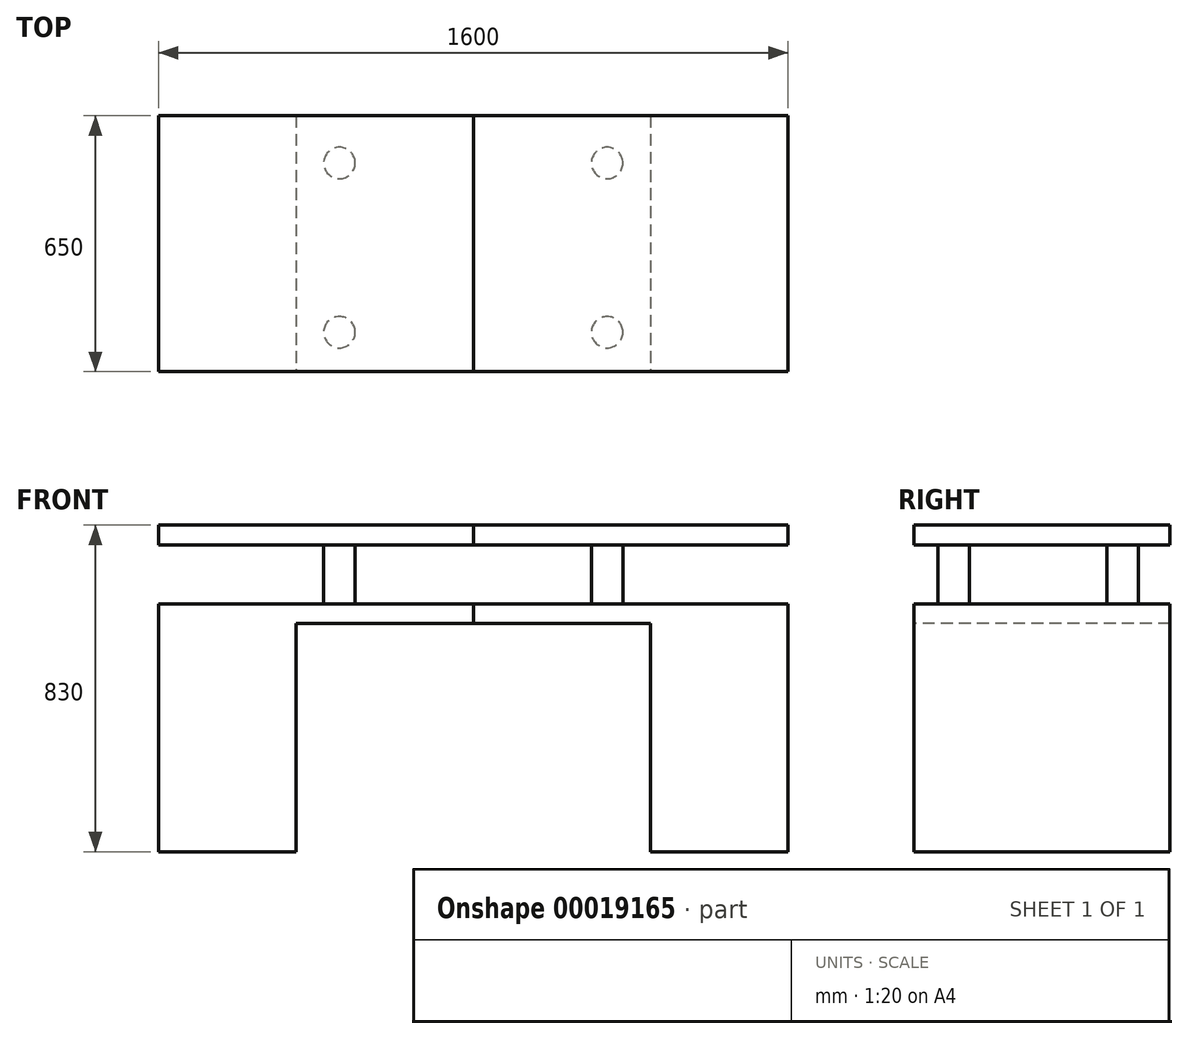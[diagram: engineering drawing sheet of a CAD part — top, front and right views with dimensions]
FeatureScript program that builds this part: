
annotation { "Feature Type Name" : "Feature", "Feature Type Description" : "" }
export const myFeature = defineFeature(function(context is Context, id is Id, definition is map)
    precondition{}
    {
        {
            var Q0;
            Q0=qCreatedBy(makeId("Top.planeOp"),FACE);
            var sketch = newSketch(context, id + "F0", { "sketchPlane" : qUnion([Q0])});
            skLineSegment(sketch, "E0.bottom", {"start": v(0, 0) * mm, "end": v(-800, 0) * mm});
            skLineSegment(sketch, "E0.top", {"start": v(0, -650) * mm, "end": v(-800, -650) * mm});
            skLineSegment(sketch, "E0.left", {"start": v(0, 0) * mm, "end": v(0, -650) * mm});
            skLineSegment(sketch, "E0.right", {"start": v(-800, 0) * mm, "end": v(-800, -650) * mm});
            skSolve(sketch);
        }
        {
            var Q0;
            Q0=qCreatedBy(makeId("Top.planeOp"),FACE);
            cPlane(context, id + "F1", {"entities" : qUnion([Q0]), "cplaneType" : CPlaneType.OFFSET, "offset" : 150 * mm, "width" : 150 * mm, "height" : 150 * mm});
        }
        {
            var Q0;
            Q0=qCreatedBy(id+"F1.planeOp",FACE);
            cPlane(context, id + "F2", {"entities" : qUnion([Q0]), "cplaneType" : CPlaneType.OFFSET, "offset" : 50 * mm, "width" : 150 * mm, "height" : 150 * mm});
        }
        {
            var Q0;
            Q0 = qSketchRegion(id + "F0", true);
            var Q1;
            Q1=qCreatedBy(id+"F2.planeOp",FACE);
            extrude(context, id + "F3", {"entities" : qUnion([Q0]), "oppositeDirection" : true, "depth" : 50 * mm, "hasSecondDirection" : true, "secondDirectionBound" : BoundingType.UP_TO_SURFACE, "secondDirectionOppositeDirection" : false, "secondDirectionBoundEntityFace" : qUnion([Q1]), "secondDirectionDepth" : 300 * mm});
        }
        {
            var Q0;
            Q0 = qSketchRegion(id + "F0", true);
            var Q1;
            Q1=qCreatedBy(id+"F1.planeOp",FACE);
            extrude(context, id + "F4", {"entities" : qUnion([Q0]), "operationType" : NewBodyOperationType.REMOVE, "endBound" : BoundingType.UP_TO_SURFACE, "endBoundEntityFace" : qUnion([Q1]), "depth" : 250 * mm});
        }
        {
            var Q0;
            Q0=qCreatedBy(makeId("Top.planeOp"),FACE);
            var sketch = newSketch(context, id + "F5", { "sketchPlane" : qUnion([Q0])});
            skCircle(sketch, "E1", {"center": v(-340, -550) * mm, "radius": 40 * mm});
            skCircle(sketch, "E2", {"center": v(-340, -120) * mm, "radius": 40 * mm});
            skLineSegment(sketch, "E3", {"start": v(-300, -120) * mm, "end": v(-300, -550) * mm, "construction": true});
            skSolve(sketch);
        }
        {
            var Q0;
            Q0 = qSketchRegion(id + "F5", true);
            extrude(context, id + "F6", {"entities" : qUnion([Q0]), "endBound" : BoundingType.UP_TO_NEXT, "depth" : 25 * mm});
        }
        {
            var Q0;
            Q0=qCreatedBy(makeId("Top.planeOp"),FACE);
            var sketch = newSketch(context, id + "F7", { "sketchPlane" : qUnion([Q0])});
            skLineSegment(sketch, "E4.bottom", {"start": v(-800, 0) * mm, "end": v(-450, 0) * mm});
            skLineSegment(sketch, "E4.top", {"start": v(-800, -650) * mm, "end": v(-450, -650) * mm});
            skLineSegment(sketch, "E4.left", {"start": v(-800, 0) * mm, "end": v(-800, -650) * mm});
            skLineSegment(sketch, "E4.right", {"start": v(-450, 0) * mm, "end": v(-450, -650) * mm});
            skSolve(sketch);
        }
        {
            var Q0;
            Q0=qCreatedBy(id+"F2.planeOp",FACE);
            cPlane(context, id + "F8", {"entities" : qUnion([Q0]), "cplaneType" : CPlaneType.OFFSET, "offset" : 830 * mm, "oppositeDirection" : true, "width" : 150 * mm, "height" : 150 * mm});
        }
        {
            var Q0;
            Q0 = qSketchRegion(id + "F7", true);
            var Q1;
            Q1=qCreatedBy(id+"F8.planeOp",FACE);
            extrude(context, id + "F9", {"entities" : qUnion([Q0]), "operationType" : NewBodyOperationType.ADD, "endBound" : BoundingType.UP_TO_SURFACE, "oppositeDirection" : true, "endBoundEntityFace" : qUnion([Q1]), "depth" : 530 * mm});
        }
        {
            var Q0;
            Q0=makeQuery(id+"F4.boolean.opBoolean","SPLIT",BODY,{"disambiguationData":[OD(0.0)],"derivedFrom":makeQuery(id+"F3.opExtrude","SWEPT_BODY",BODY,{"disambiguationData":[OSD([sQuery(id+"F0.wireOp",EDGE,"E0.bottom"),sQuery(id+"F0.wireOp",EDGE,"E0.top"),sQuery(id+"F0.wireOp",EDGE,"E0.left"),sQuery(id+"F0.wireOp",EDGE,"E0.right")])]})});
            var Q1;
            Q1=makeQuery(id+"F4.boolean.opBoolean","SPLIT",BODY,{"disambiguationData":[OD(1.0)],"derivedFrom":makeQuery(id+"F3.opExtrude","SWEPT_BODY",BODY,{"disambiguationData":[OSD([sQuery(id+"F0.wireOp",EDGE,"E0.bottom"),sQuery(id+"F0.wireOp",EDGE,"E0.top"),sQuery(id+"F0.wireOp",EDGE,"E0.left"),sQuery(id+"F0.wireOp",EDGE,"E0.right")])]})});
            var Q2;
            Q2=makeQuery(id+"F6.opExtrude","SWEPT_BODY",BODY,{"disambiguationData":[OSD([sQuery(id+"F5.wireOp",EDGE,"E1")])]});
            var Q3;
            Q3=makeQuery(id+"F6.opExtrude","SWEPT_BODY",BODY,{"disambiguationData":[OSD([sQuery(id+"F5.wireOp",EDGE,"E2")])]});
            var Q4;
            Q4=qCreatedBy(makeId("Right.planeOp"),FACE);
            mirror(context, id + "F10", {"entities" : qUnion([Q0, Q1, Q2, Q3]), "mirrorPlane" : qUnion([Q4])});
        }
    });
